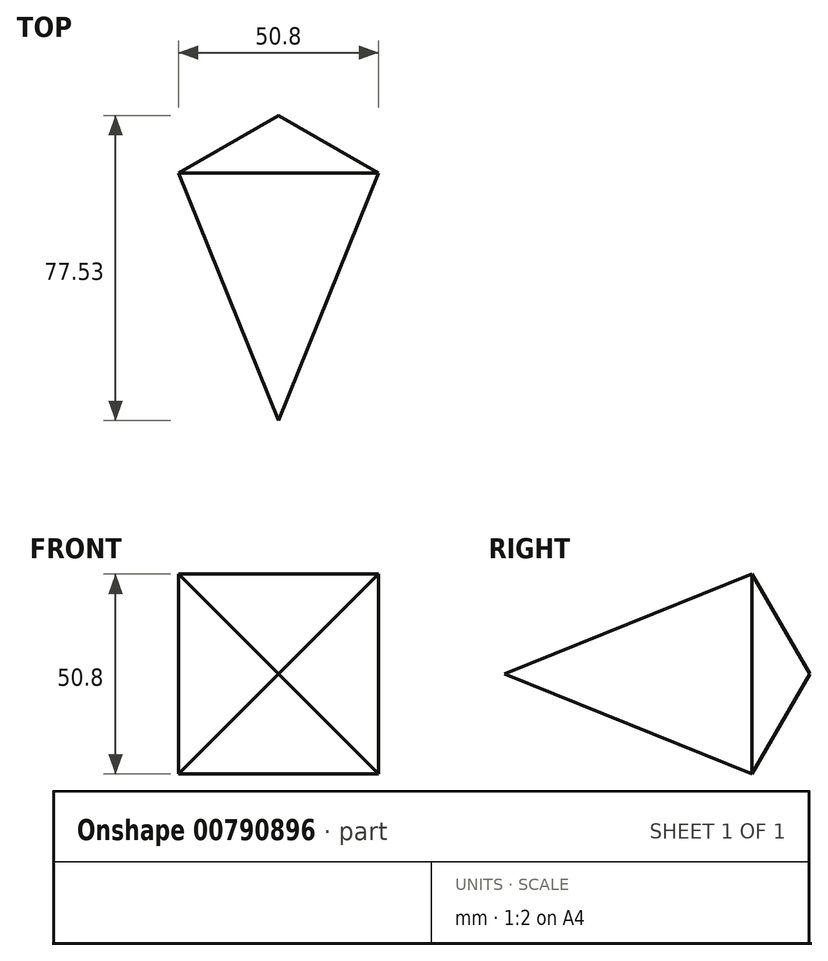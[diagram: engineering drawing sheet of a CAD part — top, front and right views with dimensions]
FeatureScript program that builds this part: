
annotation { "Feature Type Name" : "Feature", "Feature Type Description" : "" }
export const myFeature = defineFeature(function(context is Context, id is Id, definition is map)
    precondition{}
    {
        {
            var Q0;
            Q0=qCreatedBy(makeId("Front.planeOp"),FACE);
            var sketch = newSketch(context, id + "F0", { "sketchPlane" : qUnion([Q0])});
            skCircle(sketch, "E0.cCircle", {"center": v(0, 0) * mm, "radius": 25.4 * mm, "construction": true});
            skLineSegment(sketch, "E0.0", {"start": v(25.4, -25.4) * mm, "end": v(-25.4, -25.4) * mm});
            skLineSegment(sketch, "E0.1", {"start": v(-25.4, -25.4) * mm, "end": v(-25.4, 25.4) * mm});
            skLineSegment(sketch, "E0.2", {"start": v(-25.4, 25.4) * mm, "end": v(25.4, 25.4) * mm});
            skLineSegment(sketch, "E0.3", {"start": v(25.4, 25.4) * mm, "end": v(25.4, -25.4) * mm});
            skPoint(sketch, "E0.0.midPoint", {"position": v(0, -25.4) * mm});
            skSolve(sketch);
        }
        {
            var Q0;
            Q0=makeQuery(id+"F0.imprint","IMPRINT",FACE,{"disambiguationData":[TD([[makeQuery(id+"F0.imprint","IMPRINT",EDGE,{"derivedFrom":sQuery(id+"F0.wireOp",EDGE,"E0.0")}),-1.0]])]});
            extrude(context, id + "F1", {"entities" : qUnion([Q0]), "depth" : 203.2 * mm, "offsetDistance" : 25.4 * mm, "hasDraft" : true, "draftAngle" : 22 * degree, "draftPullDirection" : true});
        }
        {
            var Q0;
            Q0=makeQuery(id+"F1.opExtrude","CAP_FACE",FACE,{"disambiguationData":[OSD([sQuery(id+"F0.wireOp",EDGE,"E0.0"),sQuery(id+"F0.wireOp",EDGE,"E0.1"),sQuery(id+"F0.wireOp",EDGE,"E0.2"),sQuery(id+"F0.wireOp",EDGE,"E0.3")])],"isStart":true});
            extrude(context, id + "F2", {"entities" : qUnion([Q0]), "operationType" : NewBodyOperationType.ADD, "depth" : 203.2 * mm, "offsetDistance" : 25.4 * mm, "hasDraft" : true, "draftAngle" : 60 * degree, "draftPullDirection" : true});
        }
    });
